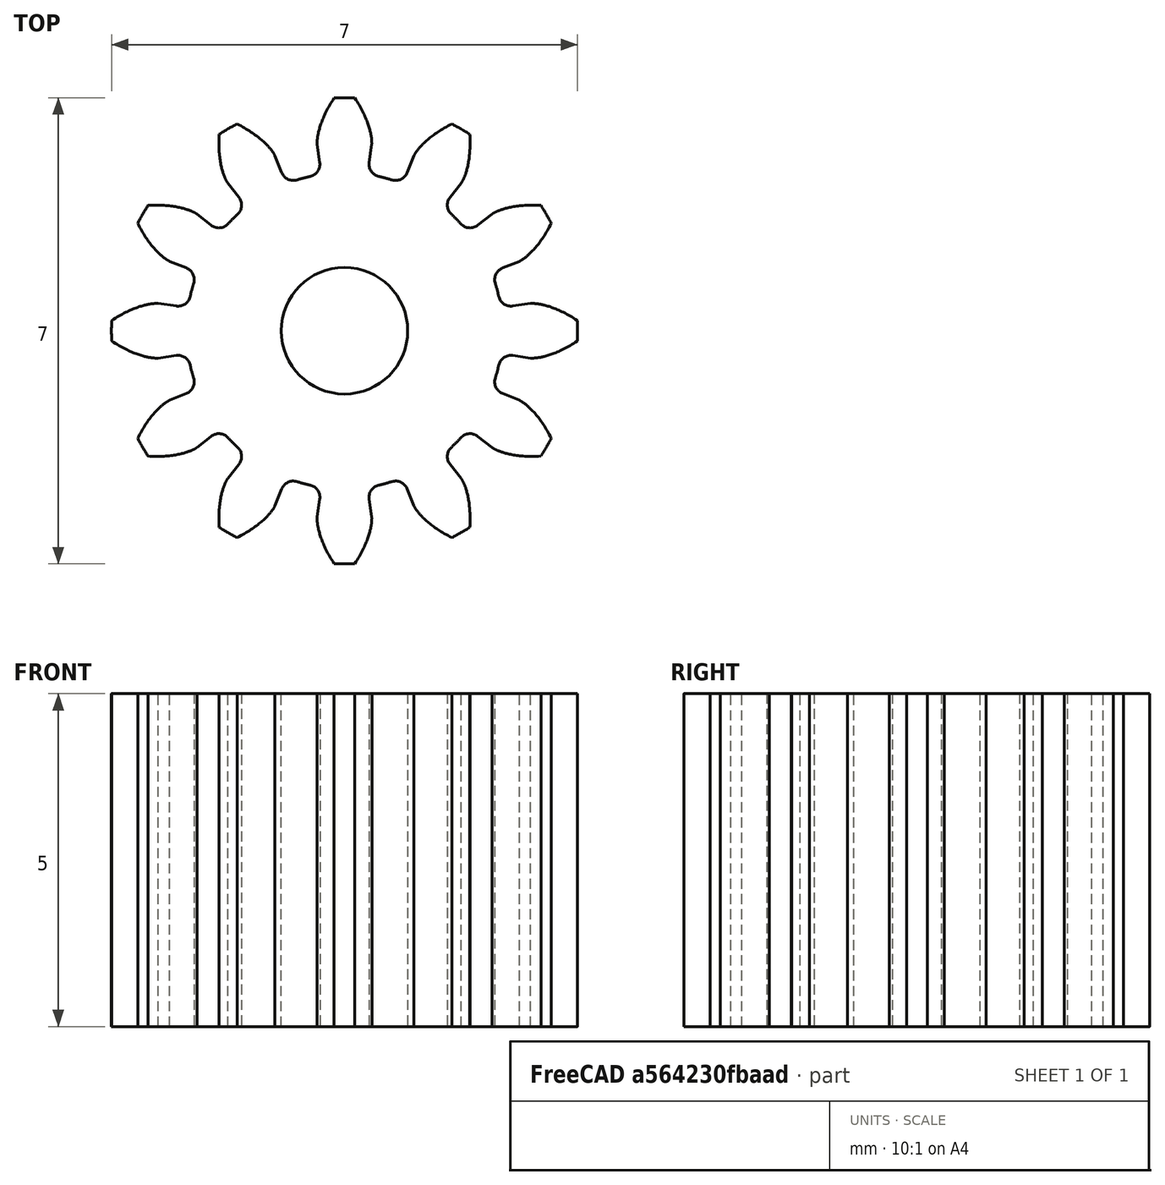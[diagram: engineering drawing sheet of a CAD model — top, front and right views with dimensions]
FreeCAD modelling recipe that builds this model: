
FCSTD DOCUMENT  (FreeCAD 0.16R6557 (Git))
Label: Gears3
License: CreativeCommons Attribution-ShareAlike
LicenseURL: http://creativecommons.org/licenses/by-sa/4.0/
objects: Part::Part2DObjectPython×1, PartDesign::Pad×1, Sketcher::SketchObject×1, PartDesign::Pocket×1, Part::Feature×1
note: 7 computed .brp shape members not serialized (recipe doc carries the construction recipe); baked Part::Feature solids carry a one-line shape summary decoded from their .brp

FEATURE [Part::Part2DObjectPython] InvoluteGear  label="12TeethGearSketch"  # Draft 2D object (typed FeaturePython)
  ExternalGear = true
  HighPrecision = true
  Modules = 0.5
  NumberOfTeeth = 12
  PressureAngle = 20
FEATURE [PartDesign::Pad] Pad  label="ExtrudedGear"
  Length = 5
  Length2 = 100
  Sketch = -> InvoluteGear
  Type = 0
FEATURE [Sketcher::SketchObject] Sketch  label="ShaftSketch"
  Placement = pos=(0,0,5) rot=(0,0,1;0rad)
  Support = -> Pad [Face122]
  sketch-geometry (1):
    g0: Circle CenterX=0 CenterY=0 CenterZ=0 NormalX=0 NormalY=0 NormalZ=1 Radius=0.95
  constraints (2):
    c: Coincident(g0,g-1)
    c: Radius(g0) = 0.95
FEATURE [PartDesign::Pocket] Pocket  label="Shaft"
  Length = 5
  Sketch = -> Sketch
  Type = 0
FEATURE [Part::Feature] Pocket001  label="Gear"
  shape: bbox 7.001 x 7.001 x 5 mm, 123 faces (baked)
